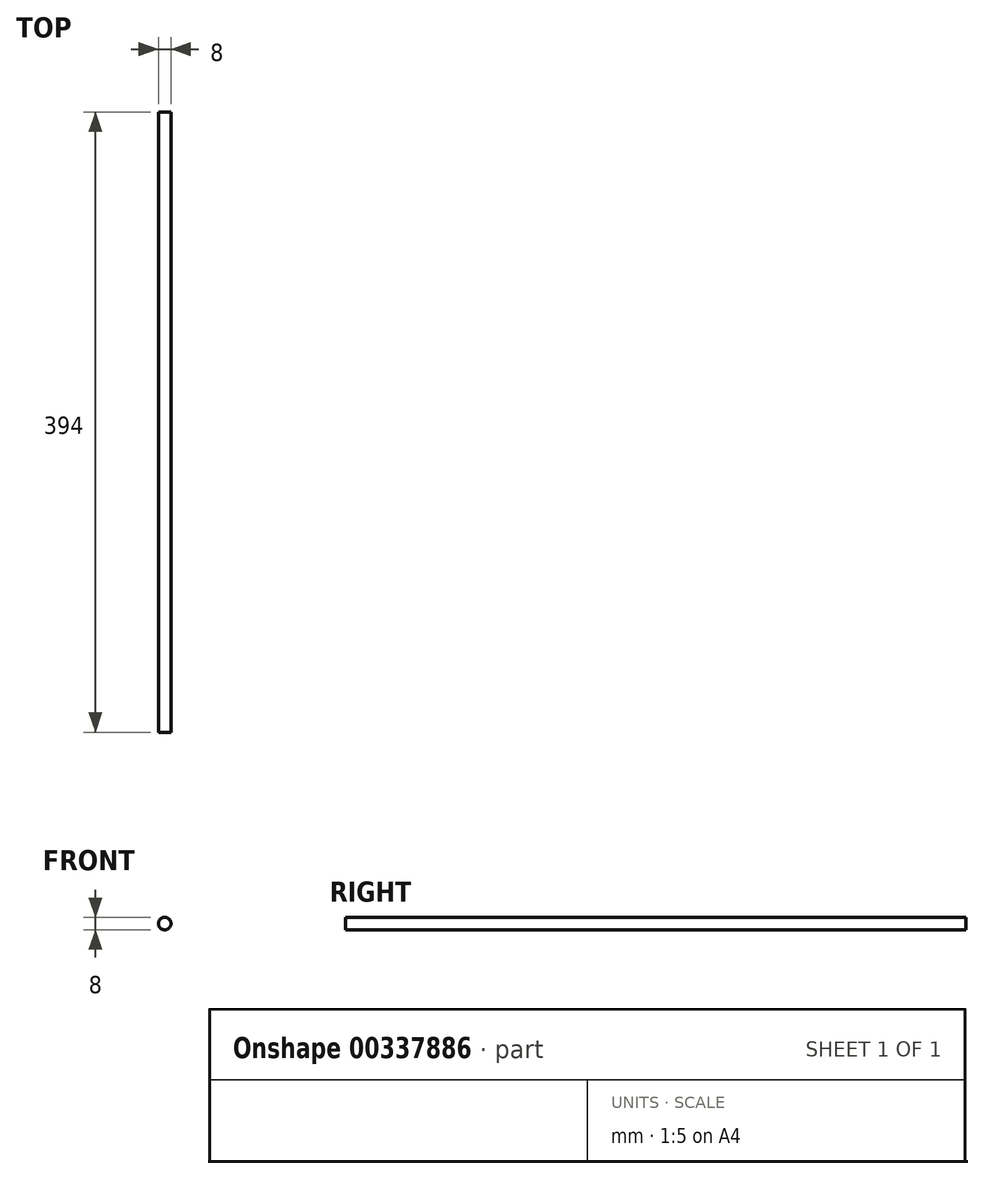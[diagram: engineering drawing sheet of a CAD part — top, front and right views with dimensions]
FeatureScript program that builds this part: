
annotation { "Feature Type Name" : "Feature", "Feature Type Description" : "" }
export const myFeature = defineFeature(function(context is Context, id is Id, definition is map)
    precondition{}
    {
        {
            var Q0;
            Q0=qCreatedBy(makeId("Front.planeOp"),FACE);
            var sketch = newSketch(context, id + "F0", { "sketchPlane" : qUnion([Q0])});
            skCircle(sketch, "E0", {"center": v(0, 0) * mm, "radius": 4 * mm});
            skSolve(sketch);
        }
        {
            var Q0;
            Q0=makeQuery(id+"F0.imprint","IMPRINT",FACE,{"disambiguationData":[TD([[makeQuery(id+"F0.imprint","IMPRINT",EDGE,{"derivedFrom":sQuery(id+"F0.wireOp",EDGE,"E0")}),1.0]])]});
            extrude(context, id + "F1", {"entities" : qUnion([Q0]), "offsetDistance" : 25 * mm, "depth" : 394 * mm});
        }
    });
